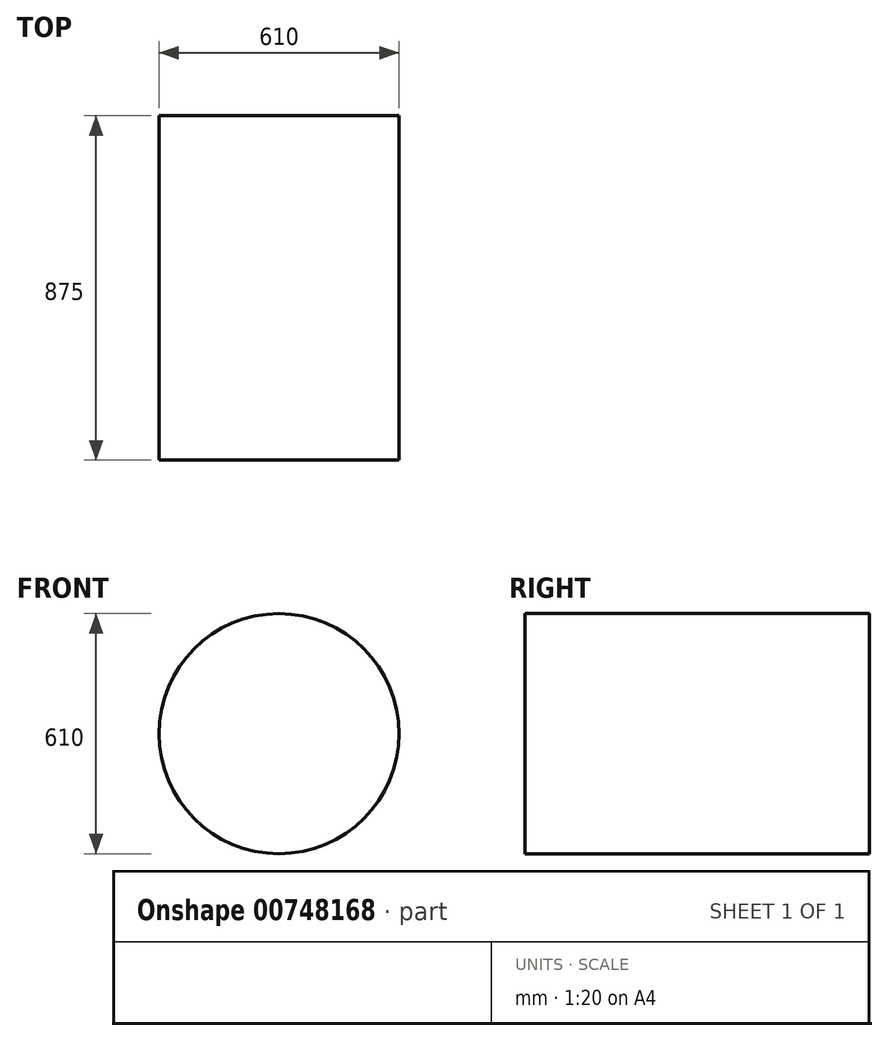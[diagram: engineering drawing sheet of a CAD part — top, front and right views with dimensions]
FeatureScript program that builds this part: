
annotation { "Feature Type Name" : "Feature", "Feature Type Description" : "" }
export const myFeature = defineFeature(function(context is Context, id is Id, definition is map)
    precondition{}
    {
        {
            var Q0;
            Q0=qCreatedBy(makeId("Front.planeOp"),FACE);
            var sketch = newSketch(context, id + "F0", { "sketchPlane" : qUnion([Q0])});
            skCircle(sketch, "E0", {"center": v(0, 0) * mm, "radius": 305 * mm});
            skSolve(sketch);
        }
        {
            var Q0;
            Q0=makeQuery(id+"F0.imprint","IMPRINT",FACE,{"disambiguationData":[TD([[makeQuery(id+"F0.imprint","IMPRINT",EDGE,{"derivedFrom":sQuery(id+"F0.wireOp",EDGE,"E0")}),1.0]])]});
            extrude(context, id + "F1", {"entities" : qUnion([Q0]), "depth" : 875 * mm, "offsetDistance" : 25 * mm});
        }
    });
